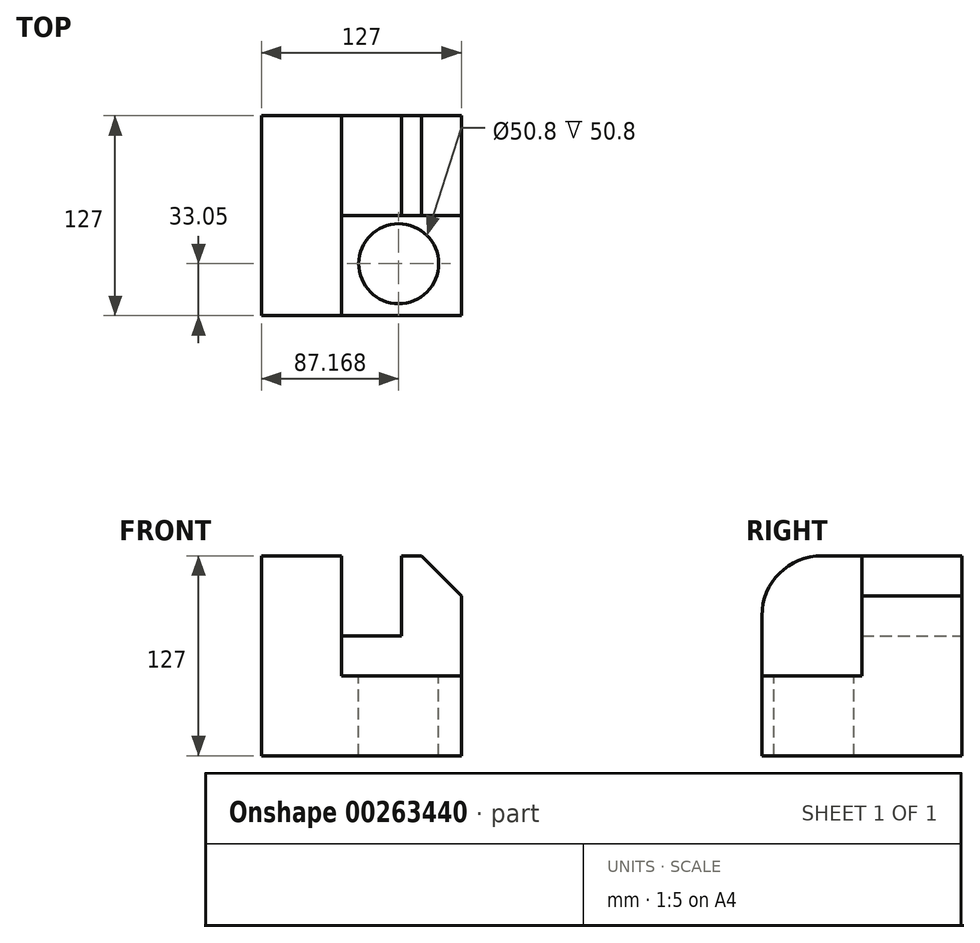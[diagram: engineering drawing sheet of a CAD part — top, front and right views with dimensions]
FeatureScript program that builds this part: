
annotation { "Feature Type Name" : "Feature", "Feature Type Description" : "" }
export const myFeature = defineFeature(function(context is Context, id is Id, definition is map)
    precondition{}
    {
        {
            var Q0;
            Q0=qCreatedBy(makeId("Front.planeOp"),FACE);
            var sketch = newSketch(context, id + "F0", { "sketchPlane" : qUnion([Q0])});
            skLineSegment(sketch, "E0.bottom", {"start": v(-62.56, 64.37) * mm, "end": v(64.44, 64.37) * mm});
            skLineSegment(sketch, "E0.top", {"start": v(-62.56, -62.63) * mm, "end": v(64.44, -62.63) * mm});
            skLineSegment(sketch, "E0.left", {"start": v(-62.56, 64.37) * mm, "end": v(-62.56, -62.63) * mm});
            skLineSegment(sketch, "E0.right", {"start": v(64.44, 64.37) * mm, "end": v(64.44, -62.63) * mm});
            skSolve(sketch);
        }
        {
            var Q0;
            Q0 = qSketchRegion(id + "F0", true);
            extrude(context, id + "F1", {"entities" : qUnion([Q0]), "depth" : 127 * mm});
        }
        {
            var Q0;
            Q0=makeQuery(id+"F1.opExtrude","SWEPT_FACE",FACE,{"disambiguationData":[OSD([sQuery(id+"F0.wireOp",EDGE,"E0.bottom")])]});
            var sketch = newSketch(context, id + "F2", { "sketchPlane" : qUnion([Q0])});
            skLineSegment(sketch, "E1", {"start": v(-11.76, -127) * mm, "end": v(-11.76, -63.5) * mm});
            skLineSegment(sketch, "E2", {"start": v(-11.76, -63.5) * mm, "end": v(64.44, -63.5) * mm});
            skSolve(sketch);
        }
        {
            var Q0;
            {var subQ0=sQuery(id+"F2.wireOp",EDGE,"E1");Q0=makeQuery(id+"F2.imprint","IMPRINT",FACE,{"disambiguationData":[TD([[makeQuery(id+"F2.imprint","IMPRINT",EDGE,{"derivedFrom":subQ0}),-1.0]])]});}
            extrude(context, id + "F3", {"entities" : qUnion([Q0]), "operationType" : NewBodyOperationType.REMOVE, "oppositeDirection" : true, "depth" : 76.2 * mm});
        }
        {
            var Q0;
            Q0=makeQuery(id+"F3.boolean.opBoolean","COPY",FACE,{"derivedFrom":makeQuery(id+"F3.opExtrude","CAP_FACE",FACE,{"disambiguationData":[OSD([sQuery(id+"F0.wireOp",EDGE,"E0.bottom"),sQuery(id+"F0.wireOp",EDGE,"E0.right"),sQuery(id+"F2.wireOp",EDGE,"E1"),sQuery(id+"F2.wireOp",EDGE,"E2")])],"isStart":false})});
            var sketch = newSketch(context, id + "F4", { "sketchPlane" : qUnion([Q0])});
            skCircle(sketch, "E3", {"center": v(24.6, -93.95) * mm, "radius": 25.4 * mm});
            skSolve(sketch);
        }
        {
            var Q0;
            Q0=makeQuery(id+"F4.imprint","IMPRINT",FACE,{"disambiguationData":[TD([[makeQuery(id+"F4.imprint","IMPRINT",EDGE,{"derivedFrom":sQuery(id+"F4.wireOp",EDGE,"E3")}),1.0]])]});
            extrude(context, id + "F5", {"entities" : qUnion([Q0]), "operationType" : NewBodyOperationType.REMOVE, "oppositeDirection" : true, "depth" : 76.2 * mm});
        }
        {
            var Q0;
            Q0=makeQuery(id+"F1.opExtrude","SWEPT_FACE",FACE,{"disambiguationData":[OSD([sQuery(id+"F0.wireOp",EDGE,"E0.bottom")])]});
            var sketch = newSketch(context, id + "F6", { "sketchPlane" : qUnion([Q0])});
            skLineSegment(sketch, "E4", {"start": v(-11.76, -63.5) * mm, "end": v(-11.76, 0) * mm});
            skLineSegment(sketch, "E5", {"start": v(-11.76, 0) * mm, "end": v(26.34, 0) * mm});
            skLineSegment(sketch, "E6", {"start": v(26.34, 0) * mm, "end": v(26.34, -63.5) * mm});
            skLineSegment(sketch, "E7", {"start": v(26.34, -63.5) * mm, "end": v(-11.76, -63.5) * mm});
            skSolve(sketch);
        }
        {
            var Q0;
            Q0=makeQuery(id+"F6.imprint","IMPRINT",FACE,{"disambiguationData":[TD([[makeQuery(id+"F6.imprint","IMPRINT",EDGE,{"derivedFrom":sQuery(id+"F6.wireOp",EDGE,"E4")}),-1.0]])]});
            extrude(context, id + "F7", {"entities" : qUnion([Q0]), "operationType" : NewBodyOperationType.REMOVE, "oppositeDirection" : true, "depth" : 50.8 * mm});
        }
        {
            var Q0;
            Q0=makeQuery(id+"F1.opExtrude","CAP_EDGE",EDGE,{"disambiguationData":[OSD([sQuery(id+"F0.wireOp",EDGE,"E0.bottom")])],"isStart":false});
            fillet(context, id + "F8", {"entities" : qUnion([Q0]), "radius" : 38.1 * mm, "tangentPropagation" : true, "allowEdgeOverflow" : false});
        }
        {
            var Q0;
            Q0=makeQuery(id+"F1.opExtrude","SWEPT_EDGE",EDGE,{"disambiguationData":[OSD([sQuery(id+"F0.wireOp",EDGE,"E0.bottom"),sQuery(id+"F0.wireOp",EDGE,"E0.right")])]});
            chamfer(context, id + "F9", {"entities" : qUnion([Q0]), "width" : 25.4 * mm, "tangentPropagation" : true});
        }
    });
